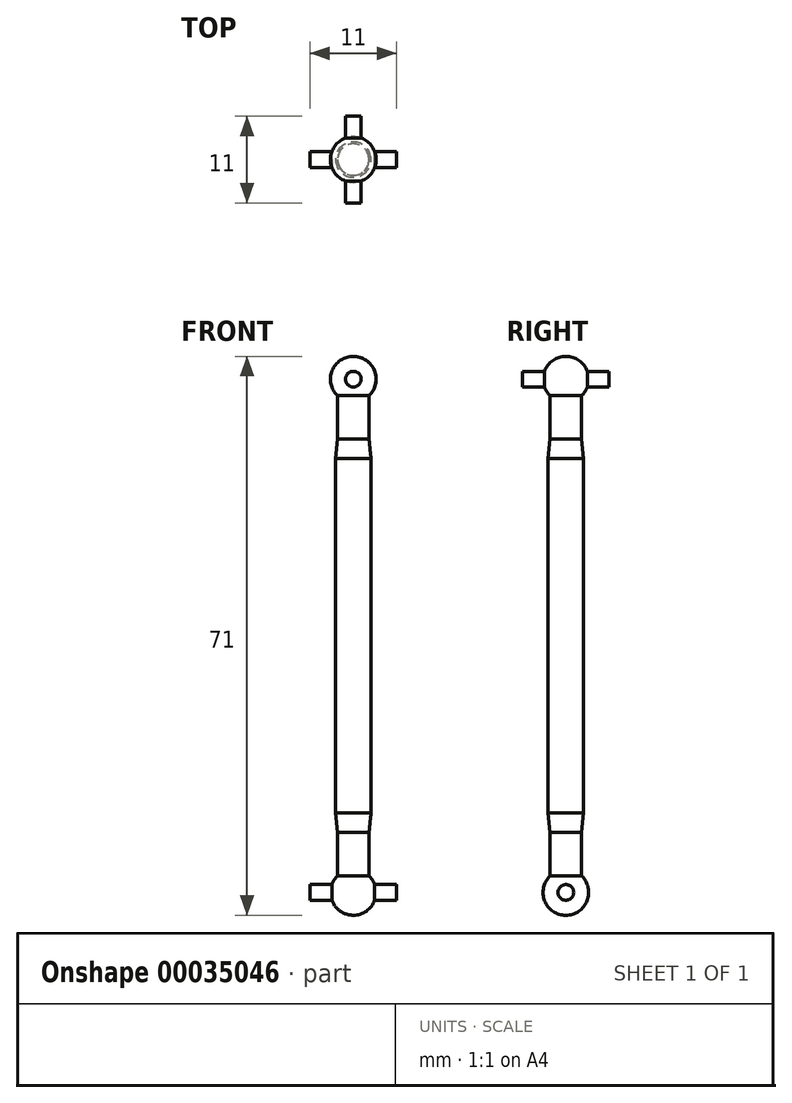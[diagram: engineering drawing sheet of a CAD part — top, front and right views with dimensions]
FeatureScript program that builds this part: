
annotation { "Feature Type Name" : "Feature", "Feature Type Description" : "" }
export const myFeature = defineFeature(function(context is Context, id is Id, definition is map)
    precondition{}
    {
        {
            var Q0;
            Q0=qCreatedBy(makeId("Front.planeOp"),FACE);
            var sketch = newSketch(context, id + "F0", { "sketchPlane" : qUnion([Q0])});
            skLineSegment(sketch, "E0", {"start": v(0, 71) * mm, "end": v(0, 0) * mm});
            skArc(sketch, "E1", {"start": v(2, 66) * mm, "mid": v(2.7, 69.18) * mm, "end": v(0, 71) * mm});
            skArc(sketch, "E2", {"start": v(0, 0) * mm, "mid": v(2.7, 1.82) * mm, "end": v(2, 5) * mm});
            skLineSegment(sketch, "E3", {"start": v(2, 5) * mm, "end": v(2, 10.5) * mm});
            skLineSegment(sketch, "E4", {"start": v(2, 10.5) * mm, "end": v(2.25, 13) * mm});
            skLineSegment(sketch, "E5", {"start": v(2.25, 13) * mm, "end": v(2.25, 58) * mm});
            skLineSegment(sketch, "E6", {"start": v(2.25, 58) * mm, "end": v(2, 60.5) * mm});
            skLineSegment(sketch, "E7", {"start": v(2, 60.5) * mm, "end": v(2, 66) * mm});
            skLineSegment(sketch, "E8", {"start": v(2.25, 35.5) * mm, "end": v(0, 35.5) * mm, "construction": true});
            skSolve(sketch);
        }
        {
            var Q0;
            Q0 = qSketchRegion(id + "F0", true);
            var Q1;
            Q1=sQuery(id+"F0.wireOp",EDGE,"E0");
            revolve(context, id + "F1", {"entities" : qUnion([Q0]), "axis" : qUnion([Q1]), "revolveType" : RevolveType.FULL});
        }
        {
            var Q0;
            Q0=qCreatedBy(makeId("Front.planeOp"),FACE);
            var sketch = newSketch(context, id + "F2", { "sketchPlane" : qUnion([Q0])});
            skPoint(sketch, "E9.0", {"position": v(0, 68.1) * mm});
            skCircle(sketch, "E10", {"center": v(0, 68.1) * mm, "radius": 1 * mm});
            skSolve(sketch);
        }
        {
            var Q0;
            Q0 = qSketchRegion(id + "F2", true);
            extrude(context, id + "F3", {"entities" : qUnion([Q0]), "operationType" : NewBodyOperationType.ADD, "endBound" : BoundingType.SYMMETRIC, "depth" : 11 * mm});
        }
        {
            var Q0;
            Q0=qCreatedBy(makeId("Right.planeOp"),FACE);
            var sketch = newSketch(context, id + "F4", { "sketchPlane" : qUnion([Q0])});
            skPoint(sketch, "E11.0", {"position": v(0, 2.9) * mm});
            skCircle(sketch, "E12", {"center": v(0, 2.9) * mm, "radius": 1 * mm});
            skSolve(sketch);
        }
        {
            var Q0;
            Q0 = qSketchRegion(id + "F4", true);
            extrude(context, id + "F5", {"entities" : qUnion([Q0]), "operationType" : NewBodyOperationType.ADD, "endBound" : BoundingType.SYMMETRIC, "depth" : 11 * mm});
        }
    });
